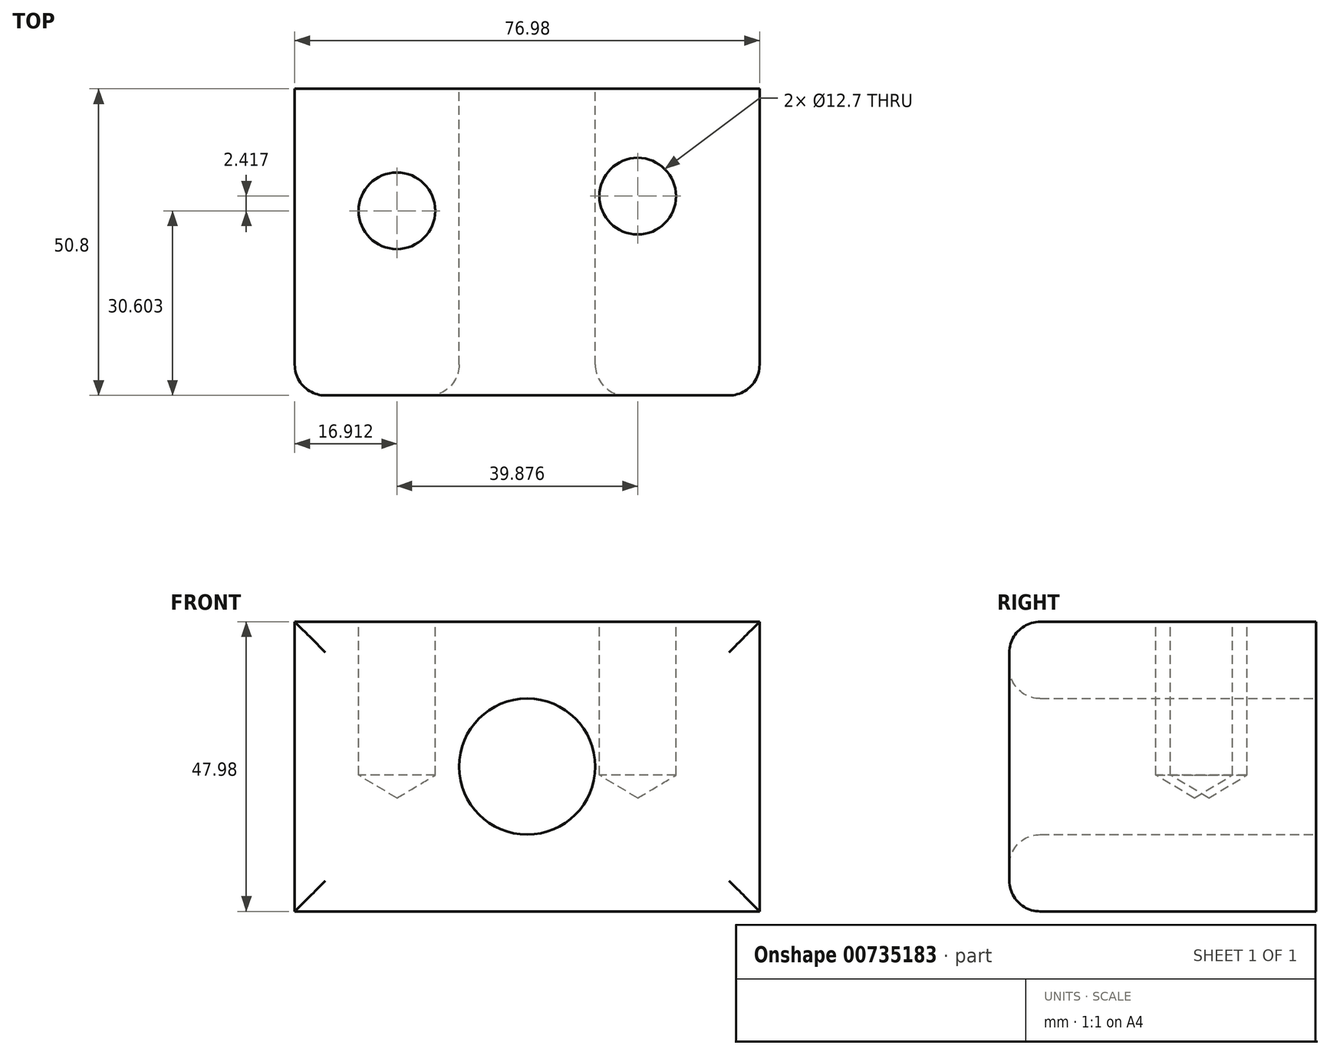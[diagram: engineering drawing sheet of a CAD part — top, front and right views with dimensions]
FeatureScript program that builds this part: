
annotation { "Feature Type Name" : "Feature", "Feature Type Description" : "" }
export const myFeature = defineFeature(function(context is Context, id is Id, definition is map)
    precondition{}
    {
        {
            var Q0;
            Q0=qCreatedBy(makeId("Front.planeOp"),FACE);
            var sketch = newSketch(context, id + "F0", { "sketchPlane" : qUnion([Q0])});
            skLineSegment(sketch, "E0.bottom", {"start": v(-38.5, 24) * mm, "end": v(38.5, 24) * mm});
            skLineSegment(sketch, "E0.top", {"start": v(-38.5, -24) * mm, "end": v(38.5, -24) * mm});
            skLineSegment(sketch, "E0.left", {"start": v(-38.5, 24) * mm, "end": v(-38.5, -24) * mm});
            skLineSegment(sketch, "E0.right", {"start": v(38.5, 24) * mm, "end": v(38.5, -24) * mm});
            skPoint(sketch, "E0.middle", {"position": v(0, 0) * mm});
            skCircle(sketch, "E1", {"center": v(0, 0) * mm, "radius": 11.27 * mm});
            skSolve(sketch);
        }
        {
            var Q0;
            Q0 = qSketchRegion(id + "F0", true);
            extrude(context, id + "F1", {"entities" : qUnion([Q0]), "depth" : 50.8 * mm, "offsetDistance" : 25.4 * mm});
        }
        {
            var Q0;
            Q0=makeQuery(id+"F1.opExtrude","CAP_EDGE",EDGE,{"disambiguationData":[OSD([sQuery(id+"F0.wireOp",EDGE,"E0.right")])],"isStart":false});
            var Q1;
            Q1=makeQuery(id+"F1.opExtrude","CAP_EDGE",EDGE,{"disambiguationData":[OSD([sQuery(id+"F0.wireOp",EDGE,"E0.left")])],"isStart":false});
            var Q2;
            Q2=makeQuery(id+"F1.opExtrude","CAP_EDGE",EDGE,{"disambiguationData":[OSD([sQuery(id+"F0.wireOp",EDGE,"E0.bottom")])],"isStart":false});
            var Q3;
            Q3=makeQuery(id+"F1.opExtrude","CAP_EDGE",EDGE,{"disambiguationData":[OSD([sQuery(id+"F0.wireOp",EDGE,"E0.top")])],"isStart":false});
            var Q4;
            Q4=makeQuery(id+"F1.opExtrude","CAP_EDGE",EDGE,{"disambiguationData":[OSD([sQuery(id+"F0.wireOp",EDGE,"E1")])],"isStart":false});
            fillet(context, id + "F2", {"entities" : qUnion([Q0, Q1, Q2, Q3, Q4]), "radius" : 5.08 * mm, "tangentPropagation" : true, "allowEdgeOverflow" : false});
        }
        {
            var Q0;
            Q0=makeQuery(id+"F1.opExtrude","SWEPT_FACE",FACE,{"disambiguationData":[OSD([sQuery(id+"F0.wireOp",EDGE,"E0.bottom")])]});
            var sketch = newSketch(context, id + "F3", { "sketchPlane" : qUnion([Q0])});
            skCircle(sketch, "E2", {"center": v(-21.58, -20.2) * mm, "radius": 3.66 * mm});
            skCircle(sketch, "E3", {"center": v(18.3, -17.78) * mm, "radius": 5.7 * mm});
            skSolve(sketch);
        }
        {
            var Q0;
            Q0=sQuery(id+"F3.wireOp",VERTEX,"E2.center");
            var Q1;
            Q1=sQuery(id+"F3.wireOp",VERTEX,"E3.center");
            var Q2;
            Q2=makeQuery(id+"F1.opExtrude","SWEPT_BODY",BODY,{"disambiguationData":[OSD([sQuery(id+"F0.wireOp",EDGE,"E0.bottom"),sQuery(id+"F0.wireOp",EDGE,"E0.top"),sQuery(id+"F0.wireOp",EDGE,"E0.left"),sQuery(id+"F0.wireOp",EDGE,"E0.right"),sQuery(id+"F0.wireOp",EDGE,"E1")])]});
            hole(context, id + "F4", {"style" : HoleStyle.C_BORE, "endStyle" : HoleEndStyle.BLIND, "holeDiameter" : 12.7 * mm, "cBoreDiameter" : 12.7 * mm, "cBoreDepth" : 6.35 * mm, "majorDiameter" : 6.35 * mm, "holeDepth" : 25.4 * mm, "isTappedThrough" : true, "tappedDepth" : 12.7 * mm, "tapClearance" : 3, "locations" : qUnion([Q0, Q1]), "scope" : qUnion([Q2])});
        }
    });
